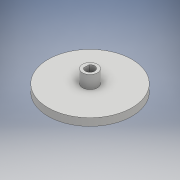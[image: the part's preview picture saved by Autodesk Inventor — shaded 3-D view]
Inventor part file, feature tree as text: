
AUTODESK INVENTOR PART (.ipt)
format: ipt  version: 2017 (Build 210142000, 142)  size: 226,816 bytes
history: native  units: mm
features: sketch x11, extrude x10, revolve x1
ambient origin geometry x8: Origin, YZ Plane, XZ Plane, XY Plane, X Axis, Y Axis, Z Axis, Center Point
bodies: Body1 (feature_tree)
feature tree (22):
  revolve  "Revolution2"  [1 undecoded]
  extrude  "Extrusion6"  Depth=20.0mm
  extrude  "Extrusion7"  Depth=4.0mm
  extrude  "Extrusion8"  Depth=4.0mm
  extrude  "Extrusion9"  Depth=4.0mm
  extrude  "Extrusion10"  Depth=20.0mm
  extrude  "Extrusion11"  Depth=15.0mm
  extrude  "Extrusion12"  Depth=5.0mm TaperAngle=0.0deg
  extrude  "Extrusion13"  Depth=5.0mm
  extrude  "Extrusion14"  Depth=26.0mm TaperAngle=0.0deg
  extrude  "Extrusion15"  Depth=10.0mm
  sketch  "Sketch1"  dims[d1=2.5mm d2=4.0mm]
  sketch  "Sketch6"  dims[d3=7.0mm d4=20.0mm]
  sketch  "Sketch7"  dims[d5=34.0mm d9=4.0mm]
  sketch  "Sketch8"  dims[d12=2.5mm d13=4.0mm]
  sketch  "Sketch9"  dims[d55=22.5mm d56=4.0mm]
  sketch  "Sketch10"  dims[d57=90.0deg d64=20.0mm]
  sketch  "Sketch11"  dims[d65=90.0deg d69=15.0mm]
  sketch  "Sketch12"  dims[d71=15.0mm d73=5.0mm d74=0.0mm]
  sketch  "Sketch13"  dims[d75=2.5mm d76=5.0mm]
  sketch  "Sketch14"  dims[d77=5.0mm d78=26.0mm d79=0.0mm]
  sketch  "Sketch15"  dims[d80=3.0mm d81=3.0mm d82=3.0mm d83=3.0mm d84=13.0mm d85=4.0mm d86=0.0mm d87=400.0mm d88=0.0mm d89=5.0mm d90=0.0mm d91=10.0mm d92=5.0mm d93=10.0mm d94=0.0mm d95=2.0mm d96=0.0mm d97=12.0mm d98=1.0mm d99=0.0mm d100=15.0mm d101=5.0mm d102=0.0mm d103=2.5mm d104=2.5mm d105=3.0mm d106=20.0mm d107=0.0mm]
note: 1 required parameter value undecoded (feature->parameter linkage not recoverable at this tier; creation-order binding heuristic only, values carry confidence <= 0.55)
